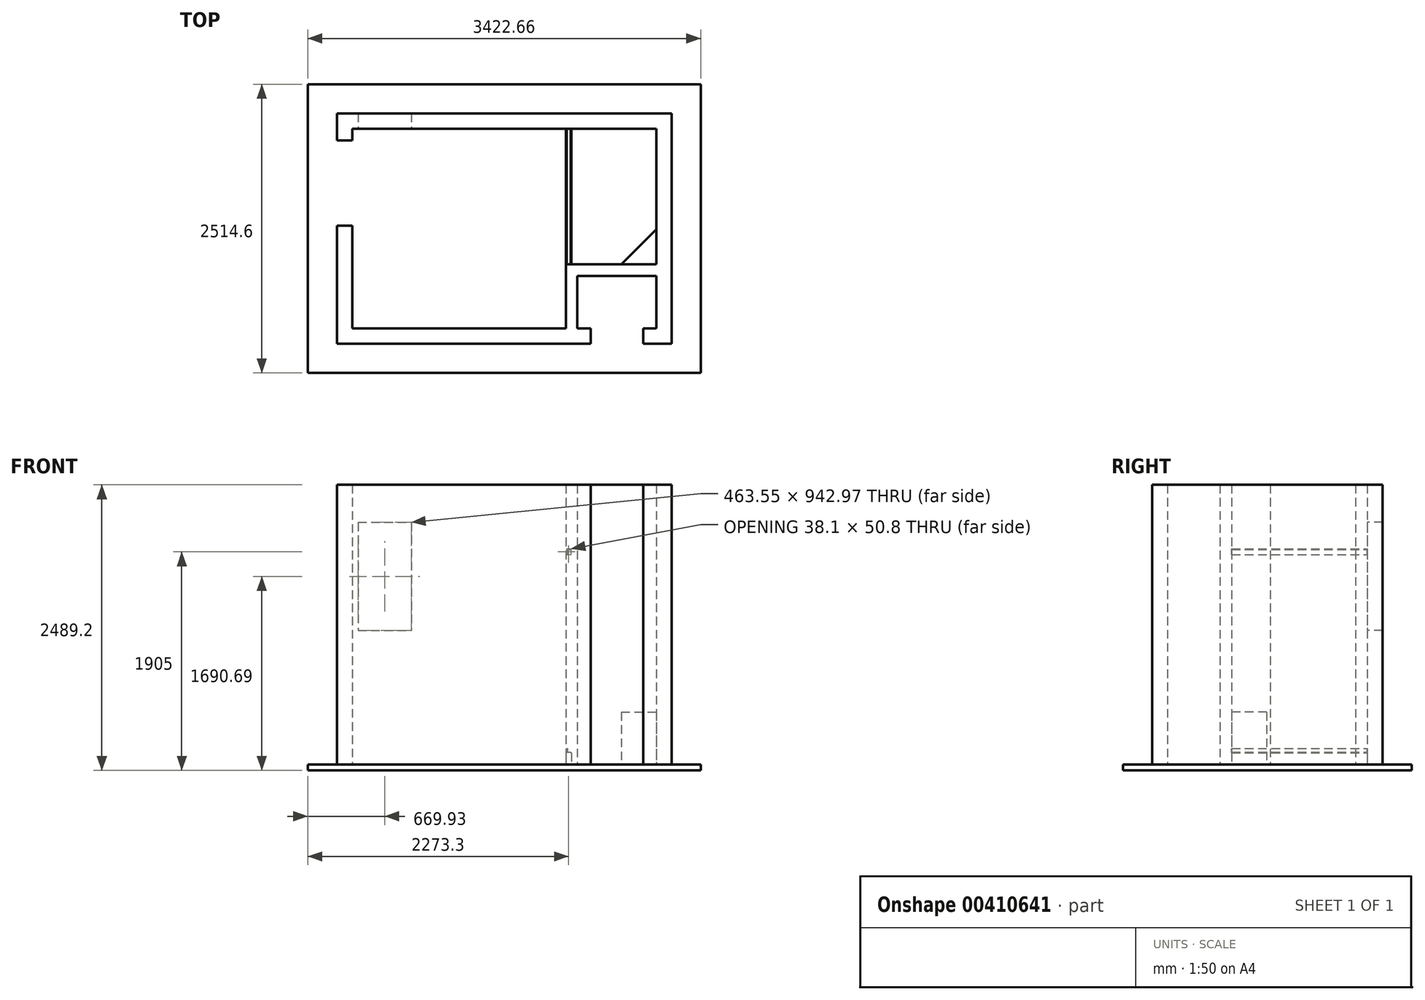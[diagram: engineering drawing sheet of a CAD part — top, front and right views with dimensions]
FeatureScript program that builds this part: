
annotation { "Feature Type Name" : "Feature", "Feature Type Description" : "" }
export const myFeature = defineFeature(function(context is Context, id is Id, definition is map)
    precondition{}
    {
        {
            var Q0;
            Q0=qCreatedBy(makeId("Top.planeOp"),FACE);
            var sketch = newSketch(context, id + "F0", { "sketchPlane" : qUnion([Q0])});
            skLineSegment(sketch, "E0.bottom", {"start": v(1323.98, -869.95) * mm, "end": v(-1323.97, -869.95) * mm});
            skLineSegment(sketch, "E0.top", {"start": v(1323.97, 869.95) * mm, "end": v(-1323.98, 869.95) * mm});
            skLineSegment(sketch, "E0.right", {"start": v(-1323.98, -869.95) * mm, "end": v(-1323.98, 869.95) * mm});
            skPoint(sketch, "E0.middle", {"position": v(0, 0) * mm});
            skLineSegment(sketch, "E1.bottom", {"start": v(1323.97, 869.95) * mm, "end": v(1323.97, 869.95) * mm});
            skLineSegment(sketch, "E1.right", {"start": v(1323.97, 869.95) * mm, "end": v(1323.98, -869.95) * mm});
            skLineSegment(sketch, "E2.0", {"start": v(1457.33, -1003.3) * mm, "end": v(-1457.33, -1003.3) * mm});
            skLineSegment(sketch, "E2.1", {"start": v(-1457.33, -1003.3) * mm, "end": v(-1457.33, 1003.3) * mm});
            skLineSegment(sketch, "E2.2", {"start": v(1457.33, 1003.3) * mm, "end": v(-1457.33, 1003.3) * mm});
            skLineSegment(sketch, "E3", {"start": v(1457.33, 1003.3) * mm, "end": v(1457.33, -1003.3) * mm});
            skLineSegment(sketch, "E4", {"start": v(752.48, -869.95) * mm, "end": v(752.48, -1003.3) * mm});
            skLineSegment(sketch, "E5", {"start": v(1209.67, -869.95) * mm, "end": v(1209.67, -1003.3) * mm});
            skLineSegment(sketch, "E6", {"start": v(-1457.33, 768.35) * mm, "end": v(-1323.98, 768.35) * mm});
            skLineSegment(sketch, "E7", {"start": v(-1457.33, 25.4) * mm, "end": v(-1323.98, 25.4) * mm});
            skLineSegment(sketch, "E8", {"start": v(536.57, 869.95) * mm, "end": v(536.58, -311.15) * mm});
            skLineSegment(sketch, "E9", {"start": v(536.58, -311.15) * mm, "end": v(1323.98, -311.15) * mm});
            skLineSegment(sketch, "E10", {"start": v(1323.98, -869.95) * mm, "end": v(-1323.98, 869.95) * mm, "construction": true});
            skLineSegment(sketch, "E11", {"start": v(536.58, -311.15) * mm, "end": v(536.58, -869.95) * mm});
            skLineSegment(sketch, "E12", {"start": v(638.18, -869.95) * mm, "end": v(638.18, -412.75) * mm});
            skLineSegment(sketch, "E13", {"start": v(638.18, -412.75) * mm, "end": v(1323.98, -412.75) * mm});
            skLineSegment(sketch, "E14", {"start": v(-530.23, -869.95) * mm, "end": v(-530.23, -311.15) * mm, "construction": true});
            skLineSegment(sketch, "E15", {"start": v(536.58, -311.15) * mm, "end": v(-530.23, -311.15) * mm, "construction": true});
            skLineSegment(sketch, "E16", {"start": v(587.37, 869.95) * mm, "end": v(587.38, -311.15) * mm});
            skSolve(sketch);
        }
        {
            var Q0;
            {var subQ8=sQuery(id+"F0.wireOp",EDGE,"E0.bottom");Q0=makeQuery(id+"F0.imprint","IMPRINT",FACE,{"disambiguationData":[TD([[makeQuery(id+"F0.imprint","IMPRINT",EDGE,{"derivedFrom":subQ8}),1.0]])]});}
            var Q1;
            {var subQ0=sQuery(id+"F0.wireOp",EDGE,"E2.2");Q1=makeQuery(id+"F0.imprint","IMPRINT",FACE,{"disambiguationData":[TD([[makeQuery(id+"F0.imprint","IMPRINT",EDGE,{"derivedFrom":subQ0}),1.0]])]});}
            var Q2;
            {var subQ1=sQuery(id+"F0.wireOp",EDGE,"E9");Q2=makeQuery(id+"F0.imprint","IMPRINT",FACE,{"disambiguationData":[TD([[makeQuery(id+"F0.imprint","IMPRINT",EDGE,{"derivedFrom":subQ1}),-1.0]])]});}
            extrude(context, id + "F1", {"entities" : qUnion([Q0, Q1, Q2]), "depth" : 2438.4 * mm});
        }
        {
            var Q0;
            {var subQ0=sQuery(id+"F0.wireOp",EDGE,"E2.0");Q0=makeQuery(id+"F1.opExtrude","SWEPT_FACE",FACE,{"disambiguationData":[OSD([subQ0]),TDD([makeQuery(id+"F0.imprint","IMPRINT",EDGE,{"disambiguationData":[TD([[makeQuery(id+"F0.imprint","INTERSECT",VERTEX,{"derivedFrom":[subQ0,sQuery(id+"F0.wireOp",EDGE,"E2.1")]}),1.0]])],"derivedFrom":subQ0})])]});}
            var sketch = newSketch(context, id + "F2", { "sketchPlane" : qUnion([Q0])});
            skLineSegment(sketch, "E17.bottom", {"start": v(752.47, 2438.4) * mm, "end": v(1209.67, 2438.4) * mm});
            skLineSegment(sketch, "E17.top", {"start": v(752.47, 2032) * mm, "end": v(1209.67, 2032) * mm});
            skLineSegment(sketch, "E17.left", {"start": v(752.47, 2438.4) * mm, "end": v(752.47, 2032) * mm});
            skLineSegment(sketch, "E17.right", {"start": v(1209.67, 2438.4) * mm, "end": v(1209.67, 2032) * mm});
            skSolve(sketch);
        }
        {
            var Q0;
            {var subQ0=sQuery(id+"F0.wireOp",EDGE,"E2.1");Q0=makeQuery(id+"F1.opExtrude","SWEPT_FACE",FACE,{"disambiguationData":[OSD([subQ0]),TDD([makeQuery(id+"F0.imprint","IMPRINT",EDGE,{"disambiguationData":[TD([[makeQuery(id+"F0.imprint","INTERSECT",VERTEX,{"derivedFrom":[subQ0,sQuery(id+"F0.wireOp",EDGE,"E2.2")]}),1.0]])],"derivedFrom":subQ0})])]});}
            var sketch = newSketch(context, id + "F3", { "sketchPlane" : qUnion([Q0])});
            skLineSegment(sketch, "E18.bottom", {"start": v(-768.35, 2438.4) * mm, "end": v(-25.4, 2438.4) * mm});
            skLineSegment(sketch, "E18.top", {"start": v(-768.35, 2032) * mm, "end": v(-25.4, 2032) * mm});
            skLineSegment(sketch, "E18.left", {"start": v(-768.35, 2438.4) * mm, "end": v(-768.35, 2032) * mm});
            skLineSegment(sketch, "E18.right", {"start": v(-25.4, 2438.4) * mm, "end": v(-25.4, 2032) * mm});
            skSolve(sketch);
        }
        {
            var Q0;
            Q0=makeQuery(id+"F1.opExtrude","SWEPT_FACE",FACE,{"disambiguationData":[OSD([sQuery(id+"F0.wireOp",EDGE,"E0.top")])]});
            var sketch = newSketch(context, id + "F4", { "sketchPlane" : qUnion([Q0])});
            skLineSegment(sketch, "E19.bottom", {"start": v(-1273.18, 2111.38) * mm, "end": v(-809.63, 2111.38) * mm});
            skLineSegment(sketch, "E19.top", {"start": v(-1273.18, 1168.4) * mm, "end": v(-809.63, 1168.4) * mm});
            skLineSegment(sketch, "E19.left", {"start": v(-1273.18, 2111.38) * mm, "end": v(-1273.18, 1168.4) * mm});
            skLineSegment(sketch, "E19.right", {"start": v(-809.63, 2111.38) * mm, "end": v(-809.63, 1168.4) * mm});
            skLineSegment(sketch, "E20.bottom", {"start": v(22.23, 2111.38) * mm, "end": v(485.78, 2111.38) * mm, "construction": true});
            skLineSegment(sketch, "E20.top", {"start": v(22.23, 1168.4) * mm, "end": v(485.78, 1168.4) * mm, "construction": true});
            skLineSegment(sketch, "E20.left", {"start": v(22.23, 2111.38) * mm, "end": v(22.23, 1168.4) * mm, "construction": true});
            skLineSegment(sketch, "E20.right", {"start": v(485.78, 2111.38) * mm, "end": v(485.78, 1168.4) * mm, "construction": true});
            skSolve(sketch);
        }
        {
            var Q0;
            Q0=qSketchRegion(id+"F4",true);
            extrude(context, id + "F5", {"entities" : qUnion([Q0]), "operationType" : NewBodyOperationType.REMOVE, "endBound" : BoundingType.THROUGH_ALL, "oppositeDirection" : true, "depth" : 25.4 * mm});
        }
        {
            var Q0;
            Q0=makeQuery(id+"F1.opExtrude","CAP_FACE",FACE,{"disambiguationData":[OSD([sQuery(id+"F0.wireOp",EDGE,"E0.bottom"),sQuery(id+"F0.wireOp",EDGE,"E0.top"),sQuery(id+"F0.wireOp",EDGE,"E0.left"),sQuery(id+"F0.wireOp",EDGE,"E0.right"),sQuery(id+"F0.wireOp",EDGE,"E1.bottom"),sQuery(id+"F0.wireOp",EDGE,"E1.top"),sQuery(id+"F0.wireOp",EDGE,"E1.left"),sQuery(id+"F0.wireOp",EDGE,"E1.right"),sQuery(id+"F0.wireOp",EDGE,"E2.0"),sQuery(id+"F0.wireOp",EDGE,"E2.1"),sQuery(id+"F0.wireOp",EDGE,"E2.2"),sQuery(id+"F0.wireOp",EDGE,"E3"),sQuery(id+"F0.wireOp",EDGE,"E4"),sQuery(id+"F0.wireOp",EDGE,"E5"),sQuery(id+"F0.wireOp",EDGE,"E6"),sQuery(id+"F0.wireOp",EDGE,"E7")])],"isStart":true});
            var sketch = newSketch(context, id + "F6", { "sketchPlane" : qUnion([Q0])});
            skLineSegment(sketch, "E21.2", {"start": v(1711.33, 1257.3) * mm, "end": v(-1711.33, 1257.3) * mm});
            skLineSegment(sketch, "E21.3", {"start": v(1711.33, -1257.3) * mm, "end": v(1711.33, 1257.3) * mm});
            skLineSegment(sketch, "E21.4", {"start": v(-1711.33, 1257.3) * mm, "end": v(-1711.33, -1257.3) * mm});
            skLineSegment(sketch, "E21.7", {"start": v(1711.33, -1257.3) * mm, "end": v(-1711.33, -1257.3) * mm});
            skSolve(sketch);
        }
        {
            var Q0;
            Q0=qSketchRegion(id+"F6",true);
            extrude(context, id + "F7", {"entities" : qUnion([Q0]), "operationType" : NewBodyOperationType.ADD, "depth" : 50.8 * mm});
        }
        {
            var Q0;
            {var subQ0=sQuery(id+"F0.wireOp",EDGE,"E8");Q0=makeQuery(id+"F0.imprint","IMPRINT",FACE,{"disambiguationData":[TD([[makeQuery(id+"F0.imprint","IMPRINT",EDGE,{"derivedFrom":subQ0}),1.0]])]});}
            extrude(context, id + "F8", {"entities" : qUnion([Q0]), "operationType" : NewBodyOperationType.ADD, "depth" : 101.6 * mm});
        }
        {
            var Q0;
            Q0=makeQuery(id+"F1.opExtrude","SWEPT_FACE",FACE,{"disambiguationData":[OSD([sQuery(id+"F0.wireOp",EDGE,"E0.top")])]});
            var sketch = newSketch(context, id + "F9", { "sketchPlane" : qUnion([Q0])});
            skLineSegment(sketch, "E22.bottom", {"start": v(542.93, 1879.6) * mm, "end": v(581.02, 1879.6) * mm});
            skLineSegment(sketch, "E22.left", {"start": v(542.93, 1879.6) * mm, "end": v(542.93, 1828.8) * mm});
            skLineSegment(sketch, "E23", {"start": v(542.93, 101.6) * mm, "end": v(542.93, 139.7) * mm});
            skLineSegment(sketch, "E24", {"start": v(542.93, 139.7) * mm, "end": v(549.28, 139.7) * mm});
            skLineSegment(sketch, "E25", {"start": v(549.28, 139.7) * mm, "end": v(549.28, 107.95) * mm});
            skLineSegment(sketch, "E26", {"start": v(549.28, 107.95) * mm, "end": v(581.02, 107.95) * mm});
            skLineSegment(sketch, "E27", {"start": v(581.02, 107.95) * mm, "end": v(581.02, 101.6) * mm});
            skLineSegment(sketch, "E28", {"start": v(581.02, 101.6) * mm, "end": v(542.93, 101.6) * mm});
            skLineSegment(sketch, "E29", {"start": v(542.93, 101.6) * mm, "end": v(536.58, 101.6) * mm, "construction": true});
            skLineSegment(sketch, "E30", {"start": v(581.02, 101.6) * mm, "end": v(587.38, 101.6) * mm, "construction": true});
            skLineSegment(sketch, "E31", {"start": v(542.93, 1828.8) * mm, "end": v(549.28, 1828.8) * mm});
            skLineSegment(sketch, "E32", {"start": v(549.28, 1828.8) * mm, "end": v(549.28, 1873.25) * mm});
            skLineSegment(sketch, "E33", {"start": v(549.28, 1873.25) * mm, "end": v(581.02, 1873.25) * mm});
            skLineSegment(sketch, "E34", {"start": v(581.02, 1873.25) * mm, "end": v(581.02, 1879.6) * mm});
            skLineSegment(sketch, "E35", {"start": v(542.93, 1828.8) * mm, "end": v(542.93, 139.7) * mm, "construction": true});
            skSolve(sketch);
        }
        {
            var Q0;
            Q0=makeQuery(id+"F9.imprint","IMPRINT",FACE,{"disambiguationData":[TD([[makeQuery(id+"F9.imprint","IMPRINT",EDGE,{"derivedFrom":sQuery(id+"F9.wireOp",EDGE,"E23")}),-1.0]])]});
            var Q1;
            Q1=makeQuery(id+"F9.imprint","IMPRINT",FACE,{"disambiguationData":[TD([[makeQuery(id+"F9.imprint","IMPRINT",EDGE,{"derivedFrom":sQuery(id+"F9.wireOp",EDGE,"E22.bottom")}),-1.0]])]});
            extrude(context, id + "F10", {"entities" : qUnion([Q0, Q1]), "operationType" : NewBodyOperationType.ADD, "endBound" : BoundingType.UP_TO_NEXT, "depth" : 25.4 * mm});
        }
        {
            var Q0;
            {var subQ1=sQuery(id+"F0.wireOp",EDGE,"E9");Q0=makeQuery(id+"F8.boolean.opBoolean","SPLIT",FACE,{"disambiguationData":[TD([makeQuery(id+"F1.opExtrude","SWEPT_FACE",FACE,{"disambiguationData":[OSD([subQ1])]})])],"derivedFrom":makeQuery(id+"F7.opExtrude","CAP_FACE",FACE,{"disambiguationData":[OSD([sQuery(id+"F6.wireOp",EDGE,"E21.2"),sQuery(id+"F6.wireOp",EDGE,"E21.3"),sQuery(id+"F6.wireOp",EDGE,"E21.4"),sQuery(id+"F6.wireOp",EDGE,"E21.7")])],"isStart":true})});}
            var sketch = newSketch(context, id + "F11", { "sketchPlane" : qUnion([Q0])});
            skLineSegment(sketch, "E36", {"start": v(1019.18, -311.15) * mm, "end": v(1323.98, -6.35) * mm});
            skSolve(sketch);
        }
        {
            var Q0;
            {var subQ0=sQuery(id+"F11.wireOp",EDGE,"E36");Q0=makeQuery(id+"F11.imprint","IMPRINT",FACE,{"disambiguationData":[TD([[makeQuery(id+"F11.imprint","IMPRINT",EDGE,{"derivedFrom":subQ0}),-1.0]])]});}
            extrude(context, id + "F12", {"entities" : qUnion([Q0]), "operationType" : NewBodyOperationType.ADD, "depth" : 457.2 * mm});
        }
    });
